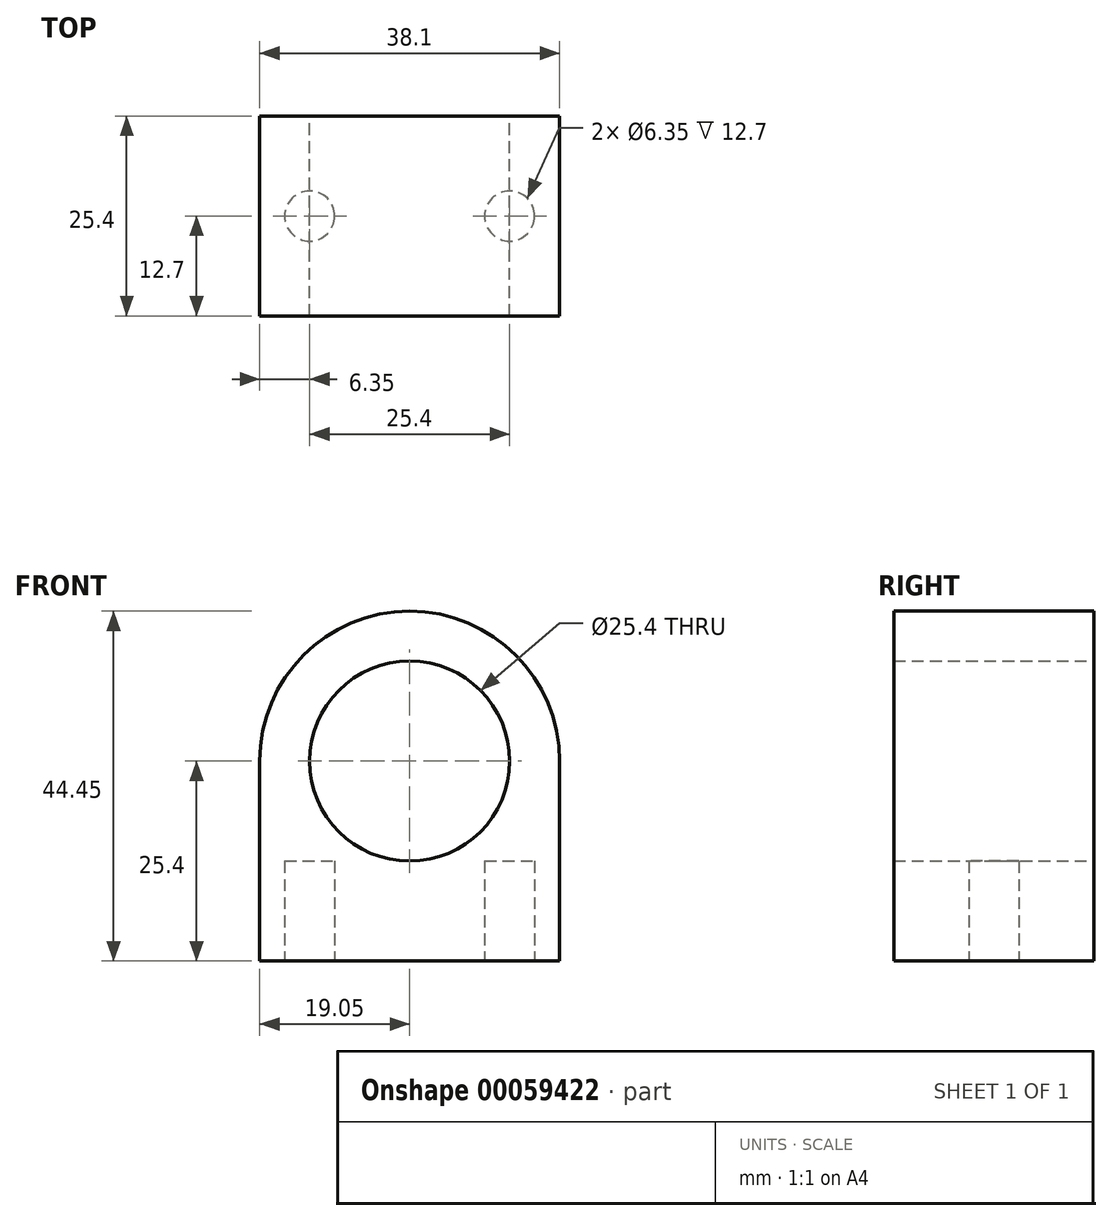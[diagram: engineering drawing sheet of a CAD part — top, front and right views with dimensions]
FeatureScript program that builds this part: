
annotation { "Feature Type Name" : "Feature", "Feature Type Description" : "" }
export const myFeature = defineFeature(function(context is Context, id is Id, definition is map)
    precondition{}
    {
        {
            var Q0;
            Q0=qCreatedBy(makeId("Front.planeOp"),FACE);
            var sketch = newSketch(context, id + "F0", { "sketchPlane" : qUnion([Q0])});
            skLineSegment(sketch, "E0", {"start": v(-41.76, 0) * mm, "end": v(49.8, 0) * mm, "construction": true});
            skCircle(sketch, "E1", {"center": v(0, 0) * mm, "radius": 12.7 * mm});
            skArc(sketch, "E2", {"start": v(19.05, 0) * mm, "mid": v(0, 19.05) * mm, "end": v(-19.05, 0) * mm});
            skLineSegment(sketch, "E3", {"start": v(-19.05, 0) * mm, "end": v(-19.05, -25.4) * mm});
            skLineSegment(sketch, "E4", {"start": v(19.05, 0) * mm, "end": v(19.05, -25.4) * mm});
            skLineSegment(sketch, "E5", {"start": v(19.05, -25.4) * mm, "end": v(-19.05, -25.4) * mm});
            skSolve(sketch);
        }
        {
            var Q0;
            Q0 = qSketchRegion(id + "F0", true);
            extrude(context, id + "F1", {"entities" : qUnion([Q0]), "depth" : 25.4 * mm});
        }
        {
            var Q0;
            Q0=makeQuery(id+"F1.opExtrude","SWEPT_FACE",FACE,{"disambiguationData":[OSD([sQuery(id+"F0.wireOp",EDGE,"E5")])]});
            var sketch = newSketch(context, id + "F2", { "sketchPlane" : qUnion([Q0])});
            skCircle(sketch, "E6", {"center": v(-12.7, 12.7) * mm, "radius": 3.18 * mm});
            skPoint(sketch, "E6.centerSnap0", {"position": v(-19.05, 12.7) * mm});
            skCircle(sketch, "E7", {"center": v(12.7, 12.7) * mm, "radius": 3.18 * mm});
            skSolve(sketch);
        }
        {
            var Q0;
            Q0 = qSketchRegion(id + "F2", true);
            extrude(context, id + "F3", {"entities" : qUnion([Q0]), "operationType" : NewBodyOperationType.REMOVE, "oppositeDirection" : true, "depth" : 12.7 * mm});
        }
    });
